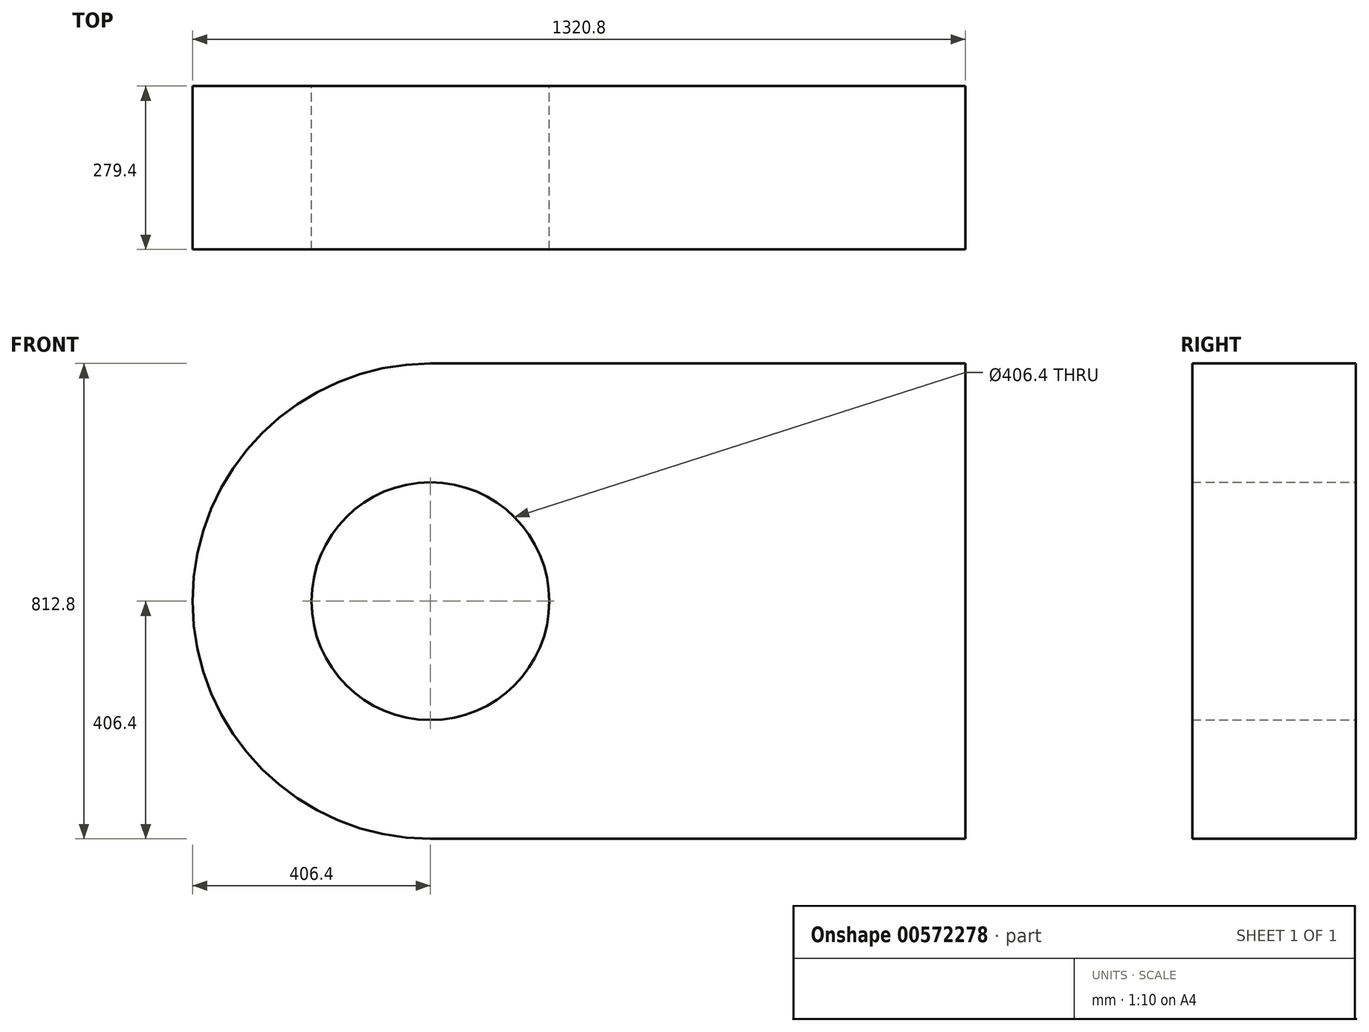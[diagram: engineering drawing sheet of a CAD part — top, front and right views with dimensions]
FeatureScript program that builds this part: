
annotation { "Feature Type Name" : "Feature", "Feature Type Description" : "" }
export const myFeature = defineFeature(function(context is Context, id is Id, definition is map)
    precondition{}
    {
        {
            var Q0;
            Q0=qCreatedBy(makeId("Front.planeOp"),FACE);
            var sketch = newSketch(context, id + "F0", { "sketchPlane" : qUnion([Q0])});
            skPoint(sketch, "E0.middle", {"position": v(203.2, 0) * mm});
            skLineSegment(sketch, "E1.top", {"start": v(0, 406.4) * mm, "end": v(914.4, 406.4) * mm});
            skLineSegment(sketch, "E1.left", {"start": v(0, 0) * mm, "end": v(0, 406.4) * mm});
            skLineSegment(sketch, "E1.right", {"start": v(914.4, 0) * mm, "end": v(914.4, 406.4) * mm});
            skLineSegment(sketch, "E2.top", {"start": v(914.4, -406.4) * mm, "end": v(0, -406.4) * mm});
            skLineSegment(sketch, "E2.left", {"start": v(914.4, 0) * mm, "end": v(914.4, -406.4) * mm});
            skLineSegment(sketch, "E2.right", {"start": v(0, 0) * mm, "end": v(0, -406.4) * mm});
            skArc(sketch, "E3", {"start": v(0, 406.4) * mm, "mid": v(-406.4, 0) * mm, "end": v(0, -406.4) * mm});
            skSolve(sketch);
        }
        {
            var Q0;
            Q0=makeQuery(id+"F0.imprint","IMPRINT",FACE,{"disambiguationData":[TD([[makeQuery(id+"F0.imprint","IMPRINT",EDGE,{"derivedFrom":sQuery(id+"F0.wireOp",EDGE,"E1.top")}),-1.0]])]});
            var sketch = newSketch(context, id + "F1", { "sketchPlane" : qUnion([Q0])});
            skCircle(sketch, "E4", {"center": v(0, 0) * mm, "radius": 203.2 * mm});
            skSolve(sketch);
        }
        {
            var Q0;
            Q0=makeQuery(id+"F0.imprint","IMPRINT",FACE,{"disambiguationData":[TD([[makeQuery(id+"F0.imprint","IMPRINT",EDGE,{"derivedFrom":sQuery(id+"F0.wireOp",EDGE,"E1.top")}),-1.0]])]});
            var Q1;
            Q1=makeQuery(id+"F0.imprint","IMPRINT",FACE,{"disambiguationData":[TD([[makeQuery(id+"F0.imprint","IMPRINT",EDGE,{"derivedFrom":sQuery(id+"F0.wireOp",EDGE,"E1.left")}),1.0]])]});
            extrude(context, id + "F2", {"entities" : qUnion([Q0, Q1]), "depth" : 279.4 * mm, "offsetDistance" : 25.4 * mm});
        }
        {
            var Q0;
            {var subQ0=sQuery(id+"F1.wireOp",EDGE,"E4");var subQ1=makeQuery(id+"F0.imprint","IMPRINT",EDGE,{"derivedFrom":sQuery(id+"F0.wireOp",EDGE,"E1.left")});var subQ2=makeQuery(id+"F1.imprint","INTERSECT",VERTEX,{"derivedFrom":[subQ1,subQ0]});Q0=makeQuery(id+"F1.imprint","IMPRINT",FACE,{"disambiguationData":[TD([[makeQuery(id+"F1.imprint","IMPRINT",EDGE,{"disambiguationData":[TD([[subQ2,-1.0]])],"derivedFrom":subQ0}),1.0]])]});}
            var Q1;
            {var subQ0=sQuery(id+"F1.wireOp",EDGE,"E4");var subQ1=makeQuery(id+"F0.imprint","IMPRINT",EDGE,{"derivedFrom":sQuery(id+"F0.wireOp",EDGE,"E1.left")});var subQ2=makeQuery(id+"F1.imprint","INTERSECT",VERTEX,{"derivedFrom":[subQ1,subQ0]});Q1=makeQuery(id+"F1.imprint","IMPRINT",FACE,{"disambiguationData":[TD([[makeQuery(id+"F1.imprint","IMPRINT",EDGE,{"disambiguationData":[TD([[subQ2,1.0]])],"derivedFrom":subQ0}),1.0]])]});}
            extrude(context, id + "F3", {"entities" : qUnion([Q0, Q1]), "operationType" : NewBodyOperationType.REMOVE, "depth" : 464.82 * mm, "offsetDistance" : 25.4 * mm});
        }
    });
